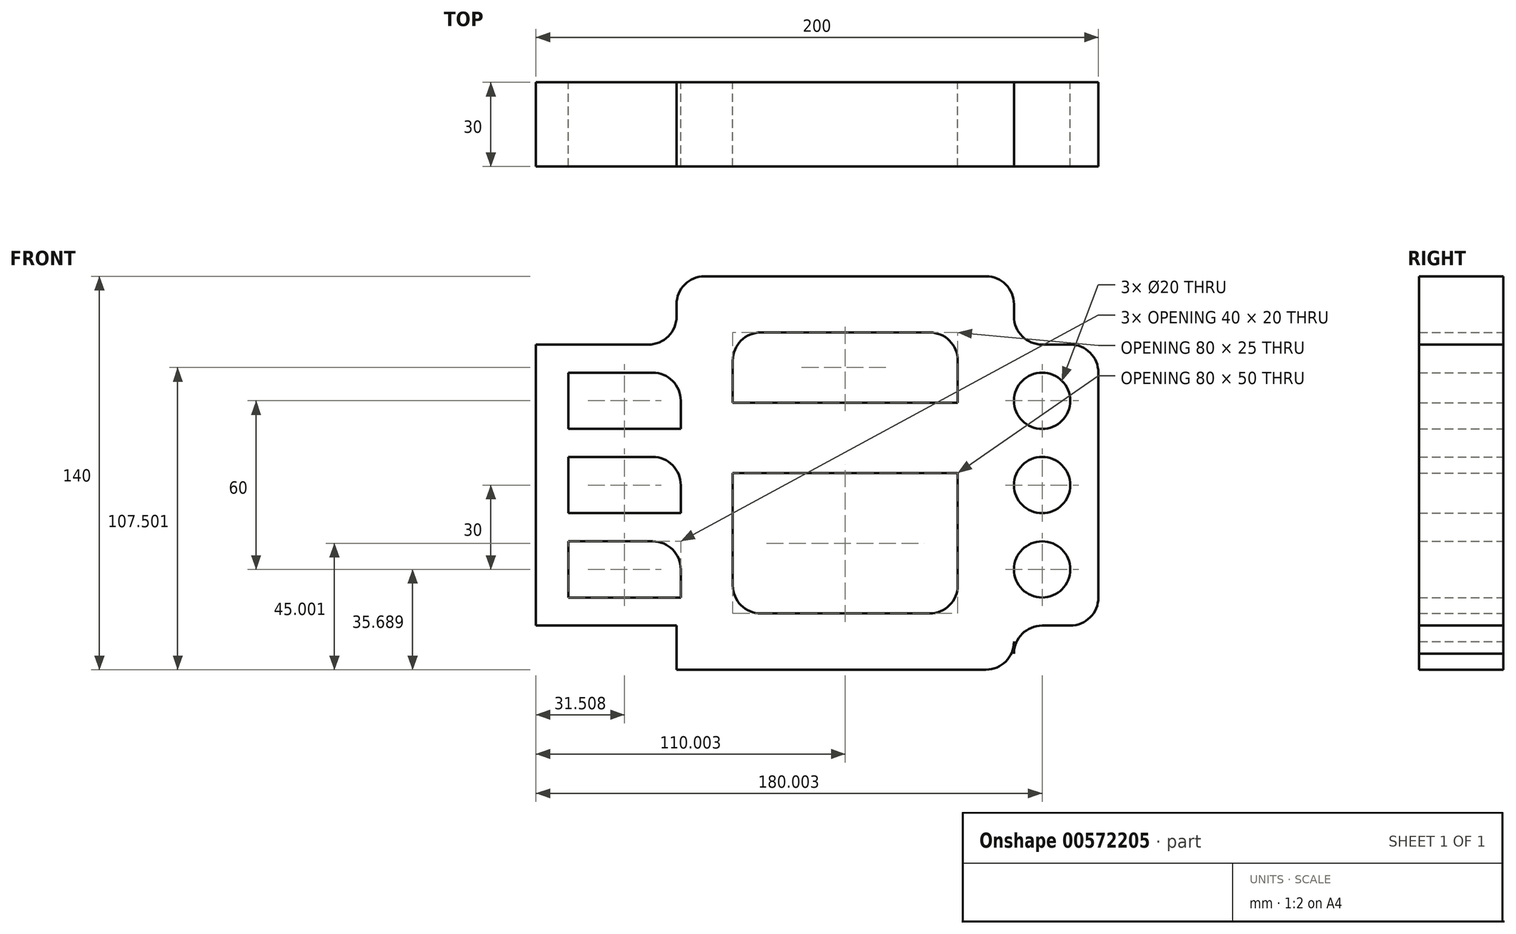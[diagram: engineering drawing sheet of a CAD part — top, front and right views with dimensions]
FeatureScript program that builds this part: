
annotation { "Feature Type Name" : "Feature", "Feature Type Description" : "" }
export const myFeature = defineFeature(function(context is Context, id is Id, definition is map)
    precondition{}
    {
        {
            var Q0;
            Q0=qCreatedBy(makeId("Front.planeOp"),FACE);
            var sketch = newSketch(context, id + "F0", { "sketchPlane" : qUnion([Q0])});
            skLineSegment(sketch, "E0", {"start": v(-53.39, 45.14) * mm, "end": v(-93.39, 45.14) * mm});
            skLineSegment(sketch, "E1", {"start": v(-93.39, 45.14) * mm, "end": v(-93.39, -54.86) * mm});
            skLineSegment(sketch, "E2", {"start": v(-93.39, -54.86) * mm, "end": v(-43.39, -54.86) * mm});
            skLineSegment(sketch, "E3", {"start": v(-43.39, -54.86) * mm, "end": v(-43.39, -70.55) * mm});
            skLineSegment(sketch, "E4", {"start": v(-43.39, -70.55) * mm, "end": v(66.61, -70.55) * mm});
            skLineSegment(sketch, "E5", {"start": v(76.61, -64.86) * mm, "end": v(76.61, -60.55) * mm});
            skLineSegment(sketch, "E6", {"start": v(86.61, -54.86) * mm, "end": v(96.61, -54.86) * mm});
            skLineSegment(sketch, "E7", {"start": v(106.61, -44.86) * mm, "end": v(106.61, 35.14) * mm});
            skLineSegment(sketch, "E8", {"start": v(96.61, 45.14) * mm, "end": v(86.61, 45.14) * mm});
            skLineSegment(sketch, "E9", {"start": v(76.61, 55.14) * mm, "end": v(76.61, 59.45) * mm});
            skLineSegment(sketch, "E10", {"start": v(66.61, 69.45) * mm, "end": v(-33.39, 69.45) * mm});
            skLineSegment(sketch, "E11", {"start": v(-43.39, 59.45) * mm, "end": v(-43.39, 55.14) * mm});
            skCircle(sketch, "E12", {"center": v(86.61, 25.14) * mm, "radius": 10 * mm});
            skCircle(sketch, "E13", {"center": v(86.61, -4.86) * mm, "radius": 10 * mm});
            skCircle(sketch, "E14", {"center": v(86.61, -34.86) * mm, "radius": 10 * mm});
            skLineSegment(sketch, "E15", {"start": v(-81.88, 35.14) * mm, "end": v(-51.88, 35.14) * mm});
            skLineSegment(sketch, "E16", {"start": v(-41.88, 25.14) * mm, "end": v(-41.88, 15.14) * mm});
            skLineSegment(sketch, "E17", {"start": v(-41.88, 15.14) * mm, "end": v(-81.88, 15.14) * mm});
            skLineSegment(sketch, "E18", {"start": v(-81.88, 15.14) * mm, "end": v(-81.88, 35.14) * mm});
            skLineSegment(sketch, "E19", {"start": v(-81.88, 5.14) * mm, "end": v(-51.88, 5.14) * mm});
            skLineSegment(sketch, "E20", {"start": v(-41.88, -4.86) * mm, "end": v(-41.88, -14.86) * mm});
            skLineSegment(sketch, "E21", {"start": v(-41.88, -14.86) * mm, "end": v(-81.88, -14.86) * mm});
            skLineSegment(sketch, "E22", {"start": v(-81.88, -14.86) * mm, "end": v(-81.88, 5.14) * mm});
            skLineSegment(sketch, "E23", {"start": v(-81.88, -24.86) * mm, "end": v(-51.88, -24.86) * mm});
            skLineSegment(sketch, "E24", {"start": v(-41.88, -34.86) * mm, "end": v(-41.88, -44.86) * mm});
            skLineSegment(sketch, "E25", {"start": v(-41.88, -44.86) * mm, "end": v(-81.88, -44.86) * mm});
            skLineSegment(sketch, "E26", {"start": v(-81.88, -44.86) * mm, "end": v(-81.88, -24.86) * mm});
            skLineSegment(sketch, "E27", {"start": v(-13.39, 49.45) * mm, "end": v(46.61, 49.45) * mm});
            skLineSegment(sketch, "E28", {"start": v(56.61, 39.45) * mm, "end": v(56.61, 24.45) * mm});
            skLineSegment(sketch, "E29", {"start": v(56.61, 24.45) * mm, "end": v(-23.39, 24.45) * mm});
            skLineSegment(sketch, "E30", {"start": v(-23.39, 24.45) * mm, "end": v(-23.39, 39.45) * mm});
            skLineSegment(sketch, "E31", {"start": v(-23.39, -0.55) * mm, "end": v(56.61, -0.55) * mm});
            skLineSegment(sketch, "E32", {"start": v(56.61, -0.55) * mm, "end": v(56.61, -40.55) * mm});
            skLineSegment(sketch, "E33", {"start": v(46.61, -50.55) * mm, "end": v(-13.39, -50.55) * mm});
            skLineSegment(sketch, "E34", {"start": v(-23.39, -40.55) * mm, "end": v(-23.39, -0.55) * mm});
            skPoint(sketch, "E35.visualSharp", {"position": v(-41.88, 35.14) * mm});
            skArc(sketch, "E35.filletArc", {"start": v(-41.88, 25.14) * mm, "mid": v(-44.81, 32.21) * mm, "end": v(-51.88, 35.14) * mm});
            skPoint(sketch, "E36.visualSharp", {"position": v(-41.88, 5.14) * mm});
            skArc(sketch, "E36.filletArc", {"start": v(-41.88, -4.86) * mm, "mid": v(-44.81, 2.21) * mm, "end": v(-51.88, 5.14) * mm});
            skPoint(sketch, "E37.visualSharp", {"position": v(-41.88, -24.86) * mm});
            skArc(sketch, "E37.filletArc", {"start": v(-41.88, -34.86) * mm, "mid": v(-44.81, -27.79) * mm, "end": v(-51.88, -24.86) * mm});
            skPoint(sketch, "E38.visualSharp", {"position": v(76.61, -54.86) * mm});
            skArc(sketch, "E38.filletArc", {"start": v(86.61, -54.86) * mm, "mid": v(79.54, -57.79) * mm, "end": v(76.61, -64.86) * mm});
            skPoint(sketch, "E39.visualSharp", {"position": v(106.61, -54.86) * mm});
            skArc(sketch, "E39.filletArc", {"start": v(96.61, -54.86) * mm, "mid": v(103.68, -51.93) * mm, "end": v(106.61, -44.86) * mm});
            skPoint(sketch, "E40.visualSharp", {"position": v(106.61, 45.14) * mm});
            skArc(sketch, "E40.filletArc", {"start": v(106.61, 35.14) * mm, "mid": v(103.68, 42.21) * mm, "end": v(96.61, 45.14) * mm});
            skPoint(sketch, "E41.visualSharp", {"position": v(76.61, 45.14) * mm});
            skArc(sketch, "E41.filletArc", {"start": v(76.61, 55.14) * mm, "mid": v(79.54, 48.07) * mm, "end": v(86.61, 45.14) * mm});
            skPoint(sketch, "E42.visualSharp", {"position": v(76.61, 69.45) * mm});
            skArc(sketch, "E42.filletArc", {"start": v(76.61, 59.45) * mm, "mid": v(73.68, 66.52) * mm, "end": v(66.61, 69.45) * mm});
            skPoint(sketch, "E43.visualSharp", {"position": v(76.61, -70.55) * mm});
            skArc(sketch, "E43.filletArc", {"start": v(66.61, -70.55) * mm, "mid": v(73.68, -67.62) * mm, "end": v(76.61, -60.55) * mm});
            skPoint(sketch, "E44.visualSharp", {"position": v(-43.39, 45.14) * mm});
            skArc(sketch, "E44.filletArc", {"start": v(-53.39, 45.14) * mm, "mid": v(-46.32, 48.07) * mm, "end": v(-43.39, 55.14) * mm});
            skPoint(sketch, "E45.visualSharp", {"position": v(-43.39, 69.45) * mm});
            skArc(sketch, "E45.filletArc", {"start": v(-33.39, 69.45) * mm, "mid": v(-40.46, 66.52) * mm, "end": v(-43.39, 59.45) * mm});
            skPoint(sketch, "E46.visualSharp", {"position": v(-23.39, 49.45) * mm});
            skArc(sketch, "E46.filletArc", {"start": v(-13.39, 49.45) * mm, "mid": v(-20.46, 46.52) * mm, "end": v(-23.39, 39.45) * mm});
            skPoint(sketch, "E47.visualSharp", {"position": v(56.61, 49.45) * mm});
            skArc(sketch, "E47.filletArc", {"start": v(56.61, 39.45) * mm, "mid": v(53.68, 46.52) * mm, "end": v(46.61, 49.45) * mm});
            skPoint(sketch, "E48.visualSharp", {"position": v(-23.39, -50.55) * mm});
            skArc(sketch, "E48.filletArc", {"start": v(-23.39, -40.55) * mm, "mid": v(-20.46, -47.62) * mm, "end": v(-13.39, -50.55) * mm});
            skPoint(sketch, "E49.visualSharp", {"position": v(56.61, -50.55) * mm});
            skArc(sketch, "E49.filletArc", {"start": v(46.61, -50.55) * mm, "mid": v(53.68, -47.62) * mm, "end": v(56.61, -40.55) * mm});
            skSolve(sketch);
        }
        {
            var Q0;
            Q0=makeQuery(id+"F0.imprint","IMPRINT",FACE,{"disambiguationData":[TD([[makeQuery(id+"F0.imprint","IMPRINT",EDGE,{"derivedFrom":sQuery(id+"F0.wireOp",EDGE,"E0")}),1.0]])]});
            extrude(context, id + "F1", {"entities" : qUnion([Q0]), "depth" : 30 * mm, "offsetDistance" : 25 * mm});
        }
    });
